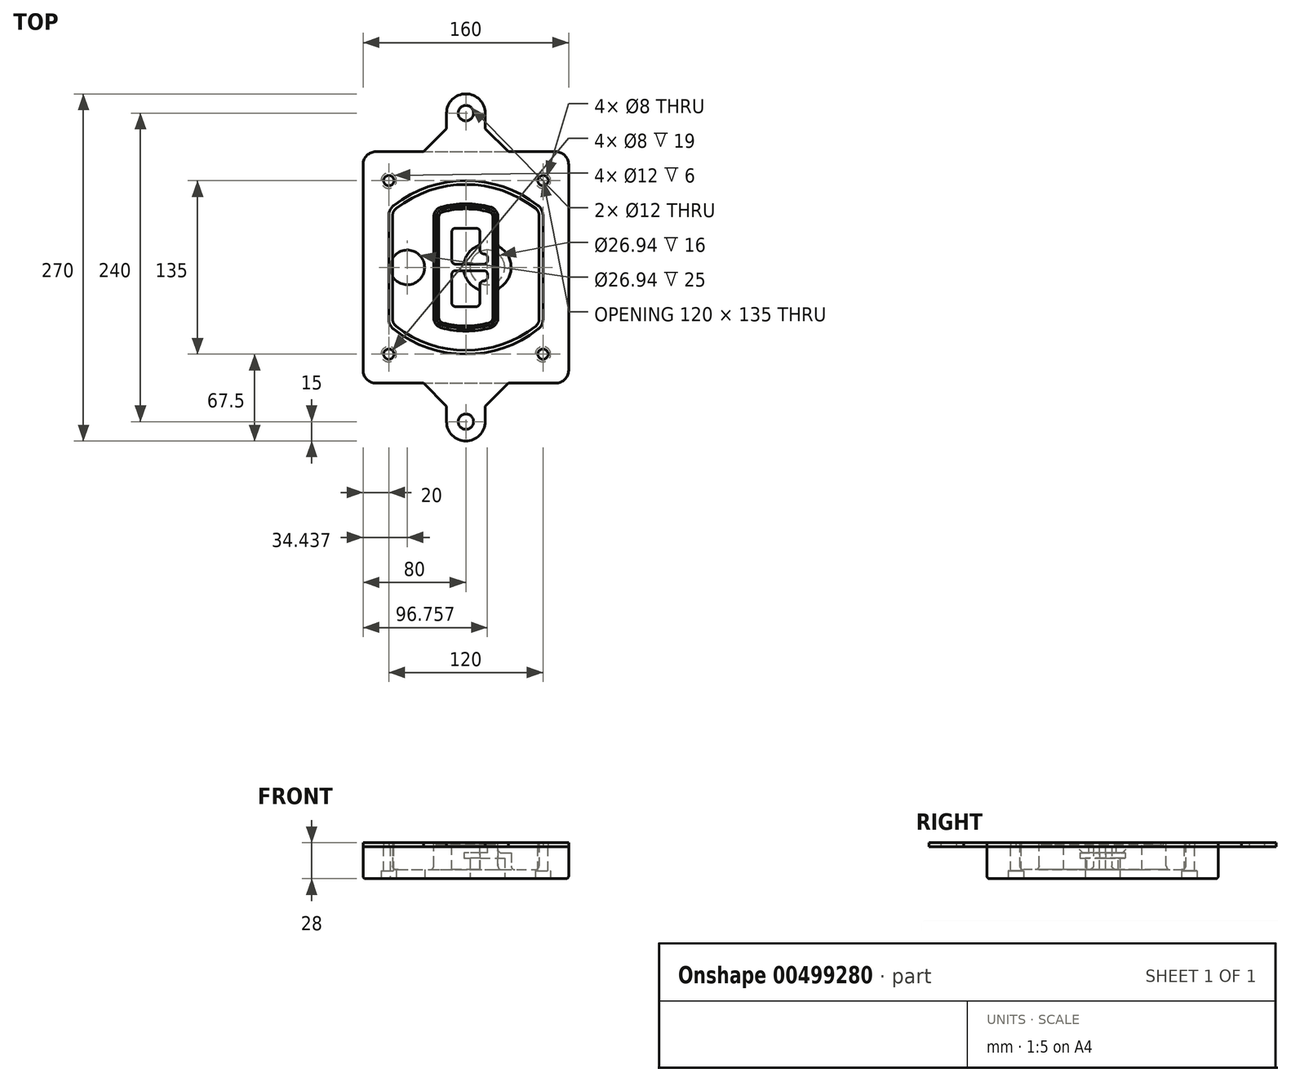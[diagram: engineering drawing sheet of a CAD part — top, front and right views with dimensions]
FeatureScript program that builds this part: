
annotation { "Feature Type Name" : "Feature", "Feature Type Description" : "" }
export const myFeature = defineFeature(function(context is Context, id is Id, definition is map)
    precondition{}
    {
        {
            var Q0;
            Q0=qCreatedBy(makeId("Top.planeOp"),FACE);
            var sketch = newSketch(context, id + "F0", { "sketchPlane" : qUnion([Q0])});
            skPoint(sketch, "E0.rect.middle", {"position": v(0, 0) * mm});
            skLineSegment(sketch, "E1.bottom", {"start": v(-70, -90) * mm, "end": v(70, -90) * mm});
            skLineSegment(sketch, "E1.top", {"start": v(-70, 90) * mm, "end": v(70, 90) * mm});
            skLineSegment(sketch, "E1.left", {"start": v(-80, -80) * mm, "end": v(-80, 80) * mm});
            skLineSegment(sketch, "E1.right", {"start": v(80, -80) * mm, "end": v(80, 80) * mm});
            skLineSegment(sketch, "E2", {"start": v(-80, 90) * mm, "end": v(80, -90) * mm, "construction": true});
            skLineSegment(sketch, "E3", {"start": v(80, 90) * mm, "end": v(-80, -90) * mm, "construction": true});
            skCircle(sketch, "E4", {"center": v(-60, 67.5) * mm, "radius": 4 * mm});
            skCircle(sketch, "E5", {"center": v(60, 67.5) * mm, "radius": 4 * mm});
            skCircle(sketch, "E6", {"center": v(60, -67.5) * mm, "radius": 4 * mm});
            skCircle(sketch, "E7", {"center": v(-60, -67.5) * mm, "radius": 4 * mm});
            skLineSegment(sketch, "E8", {"start": v(-60, 67.5) * mm, "end": v(60, 67.5) * mm, "construction": true});
            skLineSegment(sketch, "E9", {"start": v(60, 67.5) * mm, "end": v(60, -67.5) * mm, "construction": true});
            skLineSegment(sketch, "E10", {"start": v(60, -67.5) * mm, "end": v(-60, -67.5) * mm, "construction": true});
            skLineSegment(sketch, "E11", {"start": v(-60, -67.5) * mm, "end": v(-60, 67.5) * mm, "construction": true});
            skLineSegment(sketch, "E12", {"start": v(-60, 40.3) * mm, "end": v(-60, -40.3) * mm});
            skLineSegment(sketch, "E13", {"start": v(60, 40.3) * mm, "end": v(60, -40.3) * mm});
            skArc(sketch, "E14", {"start": v(56.15, 48.18) * mm, "mid": v(0, 67.5) * mm, "end": v(-56.15, 48.18) * mm});
            skArc(sketch, "E15", {"start": v(-56.15, -48.18) * mm, "mid": v(0, -67.5) * mm, "end": v(56.15, -48.18) * mm});
            skLineSegment(sketch, "E16", {"start": v(-60, 0) * mm, "end": v(60, 0) * mm, "construction": true});
            skPoint(sketch, "E17.visualSharp", {"position": v(-60, -45) * mm});
            skArc(sketch, "E17.filletArc", {"start": v(-60, -40.3) * mm, "mid": v(-58.99, -44.68) * mm, "end": v(-56.15, -48.18) * mm});
            skPoint(sketch, "E18.visualSharp", {"position": v(-60, 45) * mm});
            skArc(sketch, "E18.filletArc", {"start": v(-56.15, 48.18) * mm, "mid": v(-58.99, 44.68) * mm, "end": v(-60, 40.3) * mm});
            skPoint(sketch, "E19.visualSharp", {"position": v(60, 45) * mm});
            skArc(sketch, "E19.filletArc", {"start": v(60, 40.3) * mm, "mid": v(58.99, 44.68) * mm, "end": v(56.15, 48.18) * mm});
            skPoint(sketch, "E20.visualSharp", {"position": v(60, -45) * mm});
            skArc(sketch, "E20.filletArc", {"start": v(56.15, -48.18) * mm, "mid": v(58.99, -44.68) * mm, "end": v(60, -40.3) * mm});
            skPoint(sketch, "E21.visualSharp", {"position": v(-80, 90) * mm});
            skArc(sketch, "E21.filletArc", {"start": v(-70, 90) * mm, "mid": v(-77.07, 87.07) * mm, "end": v(-80, 80) * mm});
            skPoint(sketch, "E22.visualSharp", {"position": v(80, 90) * mm});
            skArc(sketch, "E22.filletArc", {"start": v(80, 80) * mm, "mid": v(77.07, 87.07) * mm, "end": v(70, 90) * mm});
            skPoint(sketch, "E23.visualSharp", {"position": v(80, -90) * mm});
            skArc(sketch, "E23.filletArc", {"start": v(70, -90) * mm, "mid": v(77.07, -87.07) * mm, "end": v(80, -80) * mm});
            skPoint(sketch, "E24.visualSharp", {"position": v(-80, -90) * mm});
            skArc(sketch, "E24.filletArc", {"start": v(-80, -80) * mm, "mid": v(-77.07, -87.07) * mm, "end": v(-70, -90) * mm});
            skArc(sketch, "E25.0", {"start": v(57, 40.3) * mm, "mid": v(56.3, 43.36) * mm, "end": v(54.3, 45.81) * mm});
            skLineSegment(sketch, "E25.1", {"start": v(57, 40.3) * mm, "end": v(57, -40.3) * mm});
            skArc(sketch, "E25.2", {"start": v(54.3, -45.81) * mm, "mid": v(56.3, -43.36) * mm, "end": v(57, -40.3) * mm});
            skArc(sketch, "E25.3", {"start": v(-54.3, -45.81) * mm, "mid": v(0, -64.5) * mm, "end": v(54.3, -45.81) * mm});
            skArc(sketch, "E25.4", {"start": v(-57, -40.3) * mm, "mid": v(-56.3, -43.36) * mm, "end": v(-54.3, -45.81) * mm});
            skArc(sketch, "E25.5", {"start": v(54.3, 45.81) * mm, "mid": v(0, 64.5) * mm, "end": v(-54.3, 45.81) * mm});
            skLineSegment(sketch, "E25.6", {"start": v(-57, 40.3) * mm, "end": v(-57, -40.3) * mm});
            skArc(sketch, "E25.7", {"start": v(-54.3, 45.81) * mm, "mid": v(-56.3, 43.36) * mm, "end": v(-57, 40.3) * mm});
            skArc(sketch, "E26.0", {"start": v(-58.62, 51.33) * mm, "mid": v(-62.58, 46.43) * mm, "end": v(-64, 40.3) * mm});
            skArc(sketch, "E26.1", {"start": v(58.62, 51.33) * mm, "mid": v(0, 71.5) * mm, "end": v(-58.62, 51.33) * mm});
            skArc(sketch, "E26.2", {"start": v(64, 40.3) * mm, "mid": v(62.58, 46.43) * mm, "end": v(58.62, 51.33) * mm});
            skLineSegment(sketch, "E26.3", {"start": v(64, 40.3) * mm, "end": v(64, -40.3) * mm});
            skArc(sketch, "E26.4", {"start": v(58.62, -51.33) * mm, "mid": v(62.58, -46.43) * mm, "end": v(64, -40.3) * mm});
            skLineSegment(sketch, "E26.5", {"start": v(-64, 40.3) * mm, "end": v(-64, -40.3) * mm});
            skArc(sketch, "E26.6", {"start": v(-58.62, -51.33) * mm, "mid": v(0, -71.5) * mm, "end": v(58.62, -51.33) * mm});
            skArc(sketch, "E26.7", {"start": v(-64, -40.3) * mm, "mid": v(-62.58, -46.43) * mm, "end": v(-58.62, -51.33) * mm});
            skSolve(sketch);
        }
        {
            var Q0;
            Q0=makeQuery(id+"F0.imprint","IMPRINT",FACE,{"disambiguationData":[TD([[makeQuery(id+"F0.imprint","IMPRINT",EDGE,{"derivedFrom":sQuery(id+"F0.wireOp",EDGE,"E1.bottom")}),1.0]])]});
            var Q1;
            Q1=makeQuery(id+"F0.imprint","IMPRINT",FACE,{"disambiguationData":[TD([[makeQuery(id+"F0.imprint","IMPRINT",EDGE,{"derivedFrom":sQuery(id+"F0.wireOp",EDGE,"E12")}),1.0]])]});
            var Q2;
            Q2=makeQuery(id+"F0.imprint","IMPRINT",FACE,{"disambiguationData":[TD([[makeQuery(id+"F0.imprint","IMPRINT",EDGE,{"derivedFrom":sQuery(id+"F0.wireOp",EDGE,"E25.0")}),1.0]])]});
            var Q3;
            Q3=makeQuery(id+"F0.imprint","IMPRINT",FACE,{"disambiguationData":[TD([[makeQuery(id+"F0.imprint","IMPRINT",EDGE,{"derivedFrom":sQuery(id+"F0.wireOp",EDGE,"E12")}),-1.0]])]});
            extrude(context, id + "F1", {"entities" : qUnion([Q0, Q1, Q2, Q3]), "oppositeDirection" : true, "depth" : 25 * mm});
        }
        {
            var Q0;
            Q0=makeQuery(id+"F0.imprint","IMPRINT",FACE,{"disambiguationData":[TD([[makeQuery(id+"F0.imprint","IMPRINT",EDGE,{"derivedFrom":sQuery(id+"F0.wireOp",EDGE,"E12")}),1.0]])]});
            extrude(context, id + "F2", {"entities" : qUnion([Q0]), "operationType" : NewBodyOperationType.ADD, "depth" : 3 * mm});
        }
        {
            var Q0;
            Q0=makeQuery(id+"F0.imprint","IMPRINT",FACE,{"disambiguationData":[TD([[makeQuery(id+"F0.imprint","IMPRINT",EDGE,{"derivedFrom":sQuery(id+"F0.wireOp",EDGE,"E25.0")}),1.0]])]});
            extrude(context, id + "F3", {"entities" : qUnion([Q0]), "operationType" : NewBodyOperationType.REMOVE, "oppositeDirection" : true, "depth" : 18 * mm});
        }
        {
            var Q0;
            Q0=makeQuery(id+"F2.opExtrude","CAP_FACE",FACE,{"disambiguationData":[OSD([sQuery(id+"F0.wireOp",EDGE,"E12"),sQuery(id+"F0.wireOp",EDGE,"E13"),sQuery(id+"F0.wireOp",EDGE,"E14"),sQuery(id+"F0.wireOp",EDGE,"E15"),sQuery(id+"F0.wireOp",EDGE,"E17.filletArc"),sQuery(id+"F0.wireOp",EDGE,"E18.filletArc"),sQuery(id+"F0.wireOp",EDGE,"E19.filletArc"),sQuery(id+"F0.wireOp",EDGE,"E20.filletArc"),sQuery(id+"F0.wireOp",EDGE,"E25.0"),sQuery(id+"F0.wireOp",EDGE,"E25.1"),sQuery(id+"F0.wireOp",EDGE,"E25.2"),sQuery(id+"F0.wireOp",EDGE,"E25.3"),sQuery(id+"F0.wireOp",EDGE,"E25.4"),sQuery(id+"F0.wireOp",EDGE,"E25.5"),sQuery(id+"F0.wireOp",EDGE,"E25.6"),sQuery(id+"F0.wireOp",EDGE,"E25.7")])],"isStart":false});
            var sketch = newSketch(context, id + "F4", { "sketchPlane" : qUnion([Q0])});
            skArc(sketch, "E27.0", {"start": v(-19.08, -46.97) * mm, "mid": v(0, -49.5) * mm, "end": v(19.08, -46.97) * mm});
            skArc(sketch, "E28.0", {"start": v(19.08, 46.97) * mm, "mid": v(0, 49.5) * mm, "end": v(-19.08, 46.97) * mm});
            skLineSegment(sketch, "E29", {"start": v(-25, 39.25) * mm, "end": v(-25, -39.25) * mm});
            skLineSegment(sketch, "E30", {"start": v(25, 39.25) * mm, "end": v(25, -39.25) * mm});
            skLineSegment(sketch, "E31", {"start": v(-25, 45.1) * mm, "end": v(25, 45.1) * mm, "construction": true});
            skLineSegment(sketch, "E32", {"start": v(-25, -45.1) * mm, "end": v(25, -45.1) * mm, "construction": true});
            skPoint(sketch, "E33.visualSharp", {"position": v(-25, 45.1) * mm});
            skArc(sketch, "E33.filletArc", {"start": v(-19.08, 46.97) * mm, "mid": v(-23.35, 44.11) * mm, "end": v(-25, 39.25) * mm});
            skPoint(sketch, "E34.visualSharp", {"position": v(25, 45.1) * mm});
            skArc(sketch, "E34.filletArc", {"start": v(25, 39.25) * mm, "mid": v(23.35, 44.11) * mm, "end": v(19.08, 46.97) * mm});
            skPoint(sketch, "E35.visualSharp", {"position": v(25, -45.1) * mm});
            skArc(sketch, "E35.filletArc", {"start": v(19.08, -46.97) * mm, "mid": v(23.35, -44.11) * mm, "end": v(25, -39.25) * mm});
            skPoint(sketch, "E36.visualSharp", {"position": v(-25, -45.1) * mm});
            skArc(sketch, "E36.filletArc", {"start": v(-25, -39.25) * mm, "mid": v(-23.35, -44.11) * mm, "end": v(-19.08, -46.97) * mm});
            skArc(sketch, "E37.0", {"start": v(54.3, 45.81) * mm, "mid": v(0, 64.5) * mm, "end": v(-54.3, 45.81) * mm});
            skArc(sketch, "E37.1", {"start": v(-54.3, 45.81) * mm, "mid": v(-56.3, 43.36) * mm, "end": v(-57, 40.3) * mm});
            skLineSegment(sketch, "E37.2", {"start": v(-57, 40.3) * mm, "end": v(-57, -40.3) * mm});
            skArc(sketch, "E37.3", {"start": v(-57, -40.3) * mm, "mid": v(-56.3, -43.36) * mm, "end": v(-54.3, -45.81) * mm});
            skArc(sketch, "E37.4", {"start": v(-54.3, -45.81) * mm, "mid": v(0, -64.5) * mm, "end": v(54.3, -45.81) * mm});
            skArc(sketch, "E37.5", {"start": v(54.3, -45.81) * mm, "mid": v(56.3, -43.36) * mm, "end": v(57, -40.3) * mm});
            skLineSegment(sketch, "E37.6", {"start": v(57, 40.3) * mm, "end": v(57, -40.3) * mm});
            skArc(sketch, "E37.7", {"start": v(57, 40.3) * mm, "mid": v(56.3, 43.36) * mm, "end": v(54.3, 45.81) * mm});
            skLineSegment(sketch, "E38.0", {"start": v(23, 39.25) * mm, "end": v(23, -39.25) * mm});
            skArc(sketch, "E38.1", {"start": v(18.56, -45.04) * mm, "mid": v(21.76, -42.9) * mm, "end": v(23, -39.25) * mm});
            skArc(sketch, "E38.2", {"start": v(-18.56, -45.04) * mm, "mid": v(0, -47.5) * mm, "end": v(18.56, -45.04) * mm});
            skArc(sketch, "E38.3", {"start": v(-23, -39.25) * mm, "mid": v(-21.76, -42.9) * mm, "end": v(-18.56, -45.04) * mm});
            skLineSegment(sketch, "E38.4", {"start": v(-23, 39.25) * mm, "end": v(-23, -39.25) * mm});
            skArc(sketch, "E38.5", {"start": v(23, 39.25) * mm, "mid": v(21.76, 42.9) * mm, "end": v(18.56, 45.04) * mm});
            skArc(sketch, "E38.6", {"start": v(-18.56, 45.04) * mm, "mid": v(-21.76, 42.9) * mm, "end": v(-23, 39.25) * mm});
            skArc(sketch, "E38.7", {"start": v(18.56, 45.04) * mm, "mid": v(0, 47.5) * mm, "end": v(-18.56, 45.04) * mm});
            skArc(sketch, "E39.0", {"start": v(21, 39.25) * mm, "mid": v(20.18, 41.68) * mm, "end": v(18.04, 43.1) * mm});
            skLineSegment(sketch, "E39.1", {"start": v(21, 39.25) * mm, "end": v(21, -39.25) * mm});
            skArc(sketch, "E39.2", {"start": v(18.04, -43.1) * mm, "mid": v(20.18, -41.68) * mm, "end": v(21, -39.25) * mm});
            skArc(sketch, "E39.3", {"start": v(-18.04, -43.1) * mm, "mid": v(0, -45.5) * mm, "end": v(18.04, -43.1) * mm});
            skArc(sketch, "E39.4", {"start": v(-21, -39.25) * mm, "mid": v(-20.18, -41.68) * mm, "end": v(-18.04, -43.1) * mm});
            skArc(sketch, "E39.5", {"start": v(18.04, 43.1) * mm, "mid": v(0, 45.5) * mm, "end": v(-18.04, 43.1) * mm});
            skLineSegment(sketch, "E39.6", {"start": v(-21, 39.25) * mm, "end": v(-21, -39.25) * mm});
            skArc(sketch, "E39.7", {"start": v(-18.04, 43.1) * mm, "mid": v(-20.18, 41.68) * mm, "end": v(-21, 39.25) * mm});
            skLineSegment(sketch, "E40", {"start": v(-25, 0) * mm, "end": v(25, 0) * mm, "construction": true});
            skLineSegment(sketch, "E41", {"start": v(-11, 5.5) * mm, "end": v(-11, 27.5) * mm});
            skLineSegment(sketch, "E42", {"start": v(-8, 30.5) * mm, "end": v(8, 30.5) * mm});
            skLineSegment(sketch, "E43", {"start": v(11, 27.5) * mm, "end": v(11, 13.5) * mm});
            skLineSegment(sketch, "E44", {"start": v(14, 10.5) * mm, "end": v(14, 10.5) * mm});
            skLineSegment(sketch, "E45", {"start": v(17, 7.5) * mm, "end": v(17, 5.5) * mm});
            skLineSegment(sketch, "E46", {"start": v(14, 2.5) * mm, "end": v(-8, 2.5) * mm});
            skPoint(sketch, "E47.visualSharp", {"position": v(-11, 30.5) * mm});
            skArc(sketch, "E47.filletArc", {"start": v(-8, 30.5) * mm, "mid": v(-10.12, 29.62) * mm, "end": v(-11, 27.5) * mm});
            skPoint(sketch, "E48.visualSharp", {"position": v(11, 30.5) * mm});
            skArc(sketch, "E48.filletArc", {"start": v(11, 27.5) * mm, "mid": v(10.12, 29.62) * mm, "end": v(8, 30.5) * mm});
            skPoint(sketch, "E49.visualSharp", {"position": v(11, 10.5) * mm});
            skArc(sketch, "E49.filletArc", {"start": v(11, 13.5) * mm, "mid": v(11.88, 11.38) * mm, "end": v(14, 10.5) * mm});
            skPoint(sketch, "E50.visualSharp", {"position": v(17, 10.5) * mm});
            skArc(sketch, "E50.filletArc", {"start": v(17, 7.5) * mm, "mid": v(16.12, 9.62) * mm, "end": v(14, 10.5) * mm});
            skPoint(sketch, "E51.visualSharp", {"position": v(17, 2.5) * mm});
            skArc(sketch, "E51.filletArc", {"start": v(14, 2.5) * mm, "mid": v(16.12, 3.38) * mm, "end": v(17, 5.5) * mm});
            skPoint(sketch, "E52.visualSharp", {"position": v(-11, 2.5) * mm});
            skArc(sketch, "E52.filletArc", {"start": v(-11, 5.5) * mm, "mid": v(-10.12, 3.38) * mm, "end": v(-8, 2.5) * mm});
            skLineSegment(sketch, "E53.0.MirrorCS", {"start": v(14, -2.5) * mm, "end": v(-8, -2.5) * mm});
            skArc(sketch, "E54.0.MirrorCS", {"start": v(-11, -5.5) * mm, "mid": v(-10.12, -3.38) * mm, "end": v(-8, -2.5) * mm});
            skLineSegment(sketch, "E55.0.MirrorCS", {"start": v(-11, -5.5) * mm, "end": v(-11, -27.5) * mm});
            skArc(sketch, "E56.0.MirrorCS", {"start": v(-8, -30.5) * mm, "mid": v(-10.12, -29.62) * mm, "end": v(-11, -27.5) * mm});
            skLineSegment(sketch, "E57.0.MirrorCS", {"start": v(-8, -30.5) * mm, "end": v(8, -30.5) * mm});
            skArc(sketch, "E58.0.MirrorCS", {"start": v(11, -27.5) * mm, "mid": v(10.12, -29.62) * mm, "end": v(8, -30.5) * mm});
            skLineSegment(sketch, "E59.0.MirrorCS", {"start": v(11, -27.5) * mm, "end": v(11, -13.5) * mm});
            skArc(sketch, "E60.0.MirrorCS", {"start": v(11, -13.5) * mm, "mid": v(11.88, -11.38) * mm, "end": v(14, -10.5) * mm});
            skArc(sketch, "E61.0.MirrorCS", {"start": v(17, -7.5) * mm, "mid": v(16.12, -9.62) * mm, "end": v(14, -10.5) * mm});
            skLineSegment(sketch, "E62.0.MirrorCS", {"start": v(17, -7.5) * mm, "end": v(17, -5.5) * mm});
            skArc(sketch, "E63.0.MirrorCS", {"start": v(14, -2.5) * mm, "mid": v(16.12, -3.38) * mm, "end": v(17, -5.5) * mm});
            skSolve(sketch);
        }
        {
            var Q0;
            Q0=makeQuery(id+"F4.imprint","IMPRINT",FACE,{"disambiguationData":[TD([[makeQuery(id+"F4.imprint","IMPRINT",EDGE,{"derivedFrom":sQuery(id+"F4.wireOp",EDGE,"E27.0")}),1.0]])]});
            var Q1;
            Q1=makeQuery(id+"F4.imprint","IMPRINT",FACE,{"disambiguationData":[TD([[makeQuery(id+"F4.imprint","IMPRINT",EDGE,{"derivedFrom":sQuery(id+"F4.wireOp",EDGE,"E38.0")}),-1.0]])]});
            var Q2;
            Q2=makeQuery(id+"F4.imprint","IMPRINT",FACE,{"disambiguationData":[TD([[makeQuery(id+"F4.imprint","IMPRINT",EDGE,{"derivedFrom":sQuery(id+"F4.wireOp",EDGE,"E39.0")}),1.0]])]});
            extrude(context, id + "F5", {"entities" : qUnion([Q0, Q1, Q2]), "operationType" : NewBodyOperationType.ADD, "endBound" : BoundingType.UP_TO_NEXT, "oppositeDirection" : true, "depth" : 25 * mm});
        }
        {
            var Q0;
            Q0=makeQuery(id+"F4.imprint","IMPRINT",FACE,{"disambiguationData":[TD([[makeQuery(id+"F4.imprint","IMPRINT",EDGE,{"derivedFrom":sQuery(id+"F4.wireOp",EDGE,"E38.0")}),-1.0]])]});
            extrude(context, id + "F6", {"entities" : qUnion([Q0]), "operationType" : NewBodyOperationType.REMOVE, "oppositeDirection" : true, "depth" : 2 * mm});
        }
        {
            var Q0;
            Q0=makeQuery(id+"F1.opExtrude","CAP_FACE",FACE,{"disambiguationData":[OSD([sQuery(id+"F0.wireOp",EDGE,"E1.bottom"),sQuery(id+"F0.wireOp",EDGE,"E1.top"),sQuery(id+"F0.wireOp",EDGE,"E1.left"),sQuery(id+"F0.wireOp",EDGE,"E1.right"),sQuery(id+"F0.wireOp",EDGE,"E4"),sQuery(id+"F0.wireOp",EDGE,"E5"),sQuery(id+"F0.wireOp",EDGE,"E6"),sQuery(id+"F0.wireOp",EDGE,"E7"),sQuery(id+"F0.wireOp",EDGE,"E21.filletArc"),sQuery(id+"F0.wireOp",EDGE,"E22.filletArc"),sQuery(id+"F0.wireOp",EDGE,"E23.filletArc"),sQuery(id+"F0.wireOp",EDGE,"E24.filletArc")])],"isStart":false});
            var sketch = newSketch(context, id + "F7", { "sketchPlane" : qUnion([Q0])});
            skCircle(sketch, "E64", {"center": v(16.76, 0) * mm, "radius": 13.47 * mm});
            skCircle(sketch, "E65", {"center": v(-45.56, 0) * mm, "radius": 13.47 * mm});
            skLineSegment(sketch, "E66", {"start": v(80, 0) * mm, "end": v(-80, 0) * mm});
            skCircle(sketch, "E67", {"center": v(16.76, 0) * mm, "radius": 18.47 * mm});
            skCircle(sketch, "E68", {"center": v(60, -67.5) * mm, "radius": 6 * mm});
            skCircle(sketch, "E69", {"center": v(-60, -67.5) * mm, "radius": 6 * mm});
            skCircle(sketch, "E70", {"center": v(-60, 67.5) * mm, "radius": 6 * mm});
            skCircle(sketch, "E71", {"center": v(60, 67.5) * mm, "radius": 6 * mm});
            skSolve(sketch);
        }
        {
            var Q0;
            {var subQ1=sQuery(id+"F7.wireOp",EDGE,"E66");var subQ4=sQuery(id+"F7.wireOp",EDGE,"E64");var subQ6=makeQuery(id+"F7.imprint","INTERSECT",VERTEX,{"disambiguationData":[OD(0.0)],"derivedFrom":[subQ4,subQ1]});Q0=makeQuery(id+"F7.imprint","IMPRINT",FACE,{"disambiguationData":[TD([[makeQuery(id+"F7.imprint","IMPRINT",EDGE,{"disambiguationData":[TD([[subQ6,-1.0]])],"derivedFrom":subQ4}),-1.0]])]});}
            var Q1;
            {var subQ0=sQuery(id+"F7.wireOp",EDGE,"E66");var subQ1=sQuery(id+"F7.wireOp",EDGE,"E64");var subQ3=makeQuery(id+"F7.imprint","INTERSECT",VERTEX,{"disambiguationData":[OD(0.0)],"derivedFrom":[subQ1,subQ0]});Q1=makeQuery(id+"F7.imprint","IMPRINT",FACE,{"disambiguationData":[TD([[makeQuery(id+"F7.imprint","IMPRINT",EDGE,{"disambiguationData":[TD([[subQ3,-1.0]])],"derivedFrom":subQ1}),1.0]])]});}
            var Q2;
            {var subQ0=sQuery(id+"F7.wireOp",EDGE,"E66");var subQ1=sQuery(id+"F7.wireOp",EDGE,"E64");var subQ3=makeQuery(id+"F7.imprint","INTERSECT",VERTEX,{"disambiguationData":[OD(0.0)],"derivedFrom":[subQ1,subQ0]});Q2=makeQuery(id+"F7.imprint","IMPRINT",FACE,{"disambiguationData":[TD([[makeQuery(id+"F7.imprint","IMPRINT",EDGE,{"disambiguationData":[TD([[subQ3,1.0]])],"derivedFrom":subQ1}),1.0]])]});}
            var Q3;
            {var subQ1=sQuery(id+"F7.wireOp",EDGE,"E66");var subQ4=sQuery(id+"F7.wireOp",EDGE,"E64");var subQ6=makeQuery(id+"F7.imprint","INTERSECT",VERTEX,{"disambiguationData":[OD(0.0)],"derivedFrom":[subQ4,subQ1]});Q3=makeQuery(id+"F7.imprint","IMPRINT",FACE,{"disambiguationData":[TD([[makeQuery(id+"F7.imprint","IMPRINT",EDGE,{"disambiguationData":[TD([[subQ6,1.0]])],"derivedFrom":subQ4}),-1.0]])]});}
            extrude(context, id + "F8", {"entities" : qUnion([Q0, Q1, Q2, Q3]), "operationType" : NewBodyOperationType.ADD, "oppositeDirection" : true, "depth" : 20 * mm});
        }
        {
            var Q0;
            {var subQ0=sQuery(id+"F7.wireOp",EDGE,"E66");var subQ1=sQuery(id+"F7.wireOp",EDGE,"E64");var subQ3=makeQuery(id+"F7.imprint","INTERSECT",VERTEX,{"disambiguationData":[OD(0.0)],"derivedFrom":[subQ1,subQ0]});Q0=makeQuery(id+"F7.imprint","IMPRINT",FACE,{"disambiguationData":[TD([[makeQuery(id+"F7.imprint","IMPRINT",EDGE,{"disambiguationData":[TD([[subQ3,-1.0]])],"derivedFrom":subQ1}),1.0]])]});}
            var Q1;
            {var subQ0=sQuery(id+"F7.wireOp",EDGE,"E66");var subQ1=sQuery(id+"F7.wireOp",EDGE,"E64");var subQ3=makeQuery(id+"F7.imprint","INTERSECT",VERTEX,{"disambiguationData":[OD(0.0)],"derivedFrom":[subQ1,subQ0]});Q1=makeQuery(id+"F7.imprint","IMPRINT",FACE,{"disambiguationData":[TD([[makeQuery(id+"F7.imprint","IMPRINT",EDGE,{"disambiguationData":[TD([[subQ3,1.0]])],"derivedFrom":subQ1}),1.0]])]});}
            extrude(context, id + "F9", {"entities" : qUnion([Q0, Q1]), "operationType" : NewBodyOperationType.REMOVE, "oppositeDirection" : true, "depth" : 16 * mm});
        }
        {
            var Q0;
            {var subQ0=sQuery(id+"F7.wireOp",EDGE,"E66");var subQ1=sQuery(id+"F7.wireOp",EDGE,"E65");var subQ3=makeQuery(id+"F7.imprint","INTERSECT",VERTEX,{"disambiguationData":[OD(0.0)],"derivedFrom":[subQ1,subQ0]});Q0=makeQuery(id+"F7.imprint","IMPRINT",FACE,{"disambiguationData":[TD([[makeQuery(id+"F7.imprint","IMPRINT",EDGE,{"disambiguationData":[TD([[subQ3,-1.0]])],"derivedFrom":subQ1}),1.0]])]});}
            var Q1;
            {var subQ0=sQuery(id+"F7.wireOp",EDGE,"E66");var subQ1=sQuery(id+"F7.wireOp",EDGE,"E65");var subQ3=makeQuery(id+"F7.imprint","INTERSECT",VERTEX,{"disambiguationData":[OD(0.0)],"derivedFrom":[subQ1,subQ0]});Q1=makeQuery(id+"F7.imprint","IMPRINT",FACE,{"disambiguationData":[TD([[makeQuery(id+"F7.imprint","IMPRINT",EDGE,{"disambiguationData":[TD([[subQ3,1.0]])],"derivedFrom":subQ1}),1.0]])]});}
            extrude(context, id + "F10", {"entities" : qUnion([Q0, Q1]), "operationType" : NewBodyOperationType.REMOVE, "oppositeDirection" : true, "depth" : 25 * mm});
        }
        {
            var Q0;
            Q0=makeQuery(id+"F7.imprint","IMPRINT",FACE,{"disambiguationData":[TD([[makeQuery(id+"F7.imprint","IMPRINT",EDGE,{"derivedFrom":sQuery(id+"F7.wireOp",EDGE,"E68")}),1.0]])]});
            var Q1;
            Q1=makeQuery(id+"F7.imprint","IMPRINT",FACE,{"disambiguationData":[TD([[makeQuery(id+"F7.imprint","IMPRINT",EDGE,{"derivedFrom":makeQuery(id+"F1.opExtrude","CAP_EDGE",EDGE,{"disambiguationData":[OSD([sQuery(id+"F0.wireOp",EDGE,"E5")])],"isStart":false})}),-1.0]])]});
            var Q2;
            Q2=makeQuery(id+"F7.imprint","IMPRINT",FACE,{"disambiguationData":[TD([[makeQuery(id+"F7.imprint","IMPRINT",EDGE,{"derivedFrom":sQuery(id+"F7.wireOp",EDGE,"E69")}),1.0]])]});
            var Q3;
            Q3=makeQuery(id+"F7.imprint","IMPRINT",FACE,{"disambiguationData":[TD([[makeQuery(id+"F7.imprint","IMPRINT",EDGE,{"derivedFrom":makeQuery(id+"F1.opExtrude","CAP_EDGE",EDGE,{"disambiguationData":[OSD([sQuery(id+"F0.wireOp",EDGE,"E4")])],"isStart":false})}),-1.0]])]});
            var Q4;
            Q4=makeQuery(id+"F7.imprint","IMPRINT",FACE,{"disambiguationData":[TD([[makeQuery(id+"F7.imprint","IMPRINT",EDGE,{"derivedFrom":sQuery(id+"F7.wireOp",EDGE,"E70")}),1.0]])]});
            var Q5;
            Q5=makeQuery(id+"F7.imprint","IMPRINT",FACE,{"disambiguationData":[TD([[makeQuery(id+"F7.imprint","IMPRINT",EDGE,{"derivedFrom":makeQuery(id+"F1.opExtrude","CAP_EDGE",EDGE,{"disambiguationData":[OSD([sQuery(id+"F0.wireOp",EDGE,"E7")])],"isStart":false})}),-1.0]])]});
            var Q6;
            Q6=makeQuery(id+"F7.imprint","IMPRINT",FACE,{"disambiguationData":[TD([[makeQuery(id+"F7.imprint","IMPRINT",EDGE,{"derivedFrom":sQuery(id+"F7.wireOp",EDGE,"E71")}),1.0]])]});
            var Q7;
            Q7=makeQuery(id+"F7.imprint","IMPRINT",FACE,{"disambiguationData":[TD([[makeQuery(id+"F7.imprint","IMPRINT",EDGE,{"derivedFrom":makeQuery(id+"F1.opExtrude","CAP_EDGE",EDGE,{"disambiguationData":[OSD([sQuery(id+"F0.wireOp",EDGE,"E6")])],"isStart":false})}),-1.0]])]});
            extrude(context, id + "F11", {"entities" : qUnion([Q0, Q1, Q2, Q3, Q4, Q5, Q6, Q7]), "operationType" : NewBodyOperationType.REMOVE, "oppositeDirection" : true, "depth" : 6 * mm});
        }
        {
            var Q0;
            Q0=makeQuery(id+"F9.boolean.opBoolean","COPY",FACE,{"derivedFrom":makeQuery(id+"F9.opExtrude","CAP_FACE",FACE,{"disambiguationData":[OSD([sQuery(id+"F7.wireOp",EDGE,"E64")])],"isStart":false})});
            var sketch = newSketch(context, id + "F12", { "sketchPlane" : qUnion([Q0])});
            skArc(sketch, "E72.0", {"start": v(11, 17.55) * mm, "mid": v(2.57, 11.82) * mm, "end": v(-1.54, 2.5) * mm});
            skArc(sketch, "E72.1", {"start": v(-1.54, -2.5) * mm, "mid": v(2.57, -11.82) * mm, "end": v(11, -17.55) * mm});
            skLineSegment(sketch, "E73", {"start": v(-1.54, -2.5) * mm, "end": v(14, -2.5) * mm});
            skLineSegment(sketch, "E74.0", {"start": v(14, 2.5) * mm, "end": v(-1.54, 2.5) * mm});
            skArc(sketch, "E74.1", {"start": v(14, 2.5) * mm, "mid": v(16.12, 3.38) * mm, "end": v(17, 5.5) * mm});
            skLineSegment(sketch, "E74.2", {"start": v(17, 7.5) * mm, "end": v(17, 5.5) * mm});
            skArc(sketch, "E74.3", {"start": v(17, 7.5) * mm, "mid": v(16.12, 9.62) * mm, "end": v(14, 10.5) * mm});
            skArc(sketch, "E74.4", {"start": v(11, 13.5) * mm, "mid": v(11.88, 11.38) * mm, "end": v(14, 10.5) * mm});
            skLineSegment(sketch, "E74.5", {"start": v(11, 17.55) * mm, "end": v(11, 13.5) * mm});
            skLineSegment(sketch, "E74.7", {"start": v(14, -2.5) * mm, "end": v(-1.54, -2.5) * mm});
            skArc(sketch, "E74.8", {"start": v(14, -2.5) * mm, "mid": v(16.12, -3.38) * mm, "end": v(17, -5.5) * mm});
            skLineSegment(sketch, "E74.9", {"start": v(17, -7.5) * mm, "end": v(17, -5.5) * mm});
            skArc(sketch, "E74.10", {"start": v(17, -7.5) * mm, "mid": v(16.12, -9.62) * mm, "end": v(14, -10.5) * mm});
            skArc(sketch, "E74.11", {"start": v(11, -13.5) * mm, "mid": v(11.88, -11.38) * mm, "end": v(14, -10.5) * mm});
            skLineSegment(sketch, "E74.12", {"start": v(11, -17.55) * mm, "end": v(11, -13.5) * mm});
            skPoint(sketch, "E75.orphan", {"position": v(11, -27.5) * mm});
            skPoint(sketch, "E76.orphan", {"position": v(-8, -2.5) * mm});
            skPoint(sketch, "E77.orphan", {"position": v(-8, 2.5) * mm});
            skPoint(sketch, "E78.orphan", {"position": v(11, 27.5) * mm});
            skSolve(sketch);
        }
        {
            var Q0;
            {var subQ7=sQuery(id+"F12.wireOp",EDGE,"E72.0");var subQ14=sQuery(id+"F12.wireOp",EDGE,"E72.1");var subQ16=sQuery(id+"F12.wireOp",EDGE,"E74.1");var subQ18=sQuery(id+"F12.wireOp",EDGE,"E74.8");Q0=qUnion([makeQuery(id+"F12.imprint","IMPRINT",FACE,{"disambiguationData":[TD([[makeQuery(id+"F12.imprint","IMPRINT",EDGE,{"derivedFrom":subQ7}),1.0]])]}),makeQuery(id+"F12.imprint","IMPRINT",FACE,{"disambiguationData":[TD([[makeQuery(id+"F12.imprint","IMPRINT",EDGE,{"derivedFrom":subQ14}),1.0]])]}),makeQuery(id+"F12.imprint","IMPRINT",FACE,{"disambiguationData":[TD([[makeQuery(id+"F12.imprint","IMPRINT",EDGE,{"derivedFrom":subQ16}),1.0]])]}),makeQuery(id+"F12.imprint","IMPRINT",FACE,{"disambiguationData":[TD([[makeQuery(id+"F12.imprint","IMPRINT",EDGE,{"derivedFrom":subQ18}),-1.0]])]})]);}
            var Q1;
            Q1=makeQuery(id+"F5.boolean.opBoolean","SPLIT",FACE,{"disambiguationData":[TD([makeQuery(id+"F5.opExtrude","SWEPT_FACE",FACE,{"disambiguationData":[OSD([sQuery(id+"F4.wireOp",EDGE,"E41")])]})])],"derivedFrom":makeQuery(id+"F3.boolean.opBoolean","COPY",FACE,{"derivedFrom":makeQuery(id+"F3.opExtrude","CAP_FACE",FACE,{"disambiguationData":[OSD([sQuery(id+"F0.wireOp",EDGE,"E25.0"),sQuery(id+"F0.wireOp",EDGE,"E25.1"),sQuery(id+"F0.wireOp",EDGE,"E25.2"),sQuery(id+"F0.wireOp",EDGE,"E25.3"),sQuery(id+"F0.wireOp",EDGE,"E25.4"),sQuery(id+"F0.wireOp",EDGE,"E25.5"),sQuery(id+"F0.wireOp",EDGE,"E25.6"),sQuery(id+"F0.wireOp",EDGE,"E25.7")])],"isStart":false})})});
            extrude(context, id + "F13", {"entities" : qUnion([Q0]), "operationType" : NewBodyOperationType.REMOVE, "endBound" : BoundingType.UP_TO_SURFACE, "endBoundEntityFace" : qUnion([Q1]), "depth" : 25 * mm});
        }
        {
            var Q0;
            Q0=makeQuery(id+"F3.boolean.opBoolean","COPY",EDGE,{"derivedFrom":makeQuery(id+"F3.opExtrude","CAP_EDGE",EDGE,{"disambiguationData":[OSD([sQuery(id+"F0.wireOp",EDGE,"E25.6")])],"isStart":false})});
            var Q1;
            Q1=makeQuery(id+"F8.boolean.opBoolean","INTERSECT",EDGE,{"derivedFrom":[makeQuery(id+"F5.opExtrude","SWEPT_FACE",FACE,{"disambiguationData":[OSD([sQuery(id+"F4.wireOp",EDGE,"E30")])]}),makeQuery(id+"F8.opExtrude","CAP_FACE",FACE,{"disambiguationData":[OSD([sQuery(id+"F7.wireOp",EDGE,"E67")])],"isStart":false})]});
            var Q2;
            Q2=makeQuery(id+"F8.boolean.opBoolean","INTERSECT",EDGE,{"disambiguationData":[OD(1.0)],"derivedFrom":[makeQuery(id+"F5.opExtrude","SWEPT_FACE",FACE,{"disambiguationData":[OSD([sQuery(id+"F4.wireOp",EDGE,"E30")])]}),makeQuery(id+"F8.opExtrude","SWEPT_FACE",FACE,{"disambiguationData":[OSD([sQuery(id+"F7.wireOp",EDGE,"E67")])]})]});
            var Q3;
            {var subQ0=sQuery(id+"F4.wireOp",EDGE,"E30");Q3=makeQuery(id+"F8.boolean.opBoolean","SPLIT",EDGE,{"disambiguationData":[TD([makeQuery(id+"F5.opExtrude","SWEPT_FACE",FACE,{"disambiguationData":[OSD([sQuery(id+"F4.wireOp",EDGE,"E35.filletArc")])]})])],"derivedFrom":makeQuery(id+"F5.opExtrude","CAP_EDGE",EDGE,{"disambiguationData":[OSD([subQ0])],"isStart":false})});}
            var Q4;
            {var subQ0=sQuery(id+"F0.wireOp",EDGE,"E25.7");var subQ1=sQuery(id+"F0.wireOp",EDGE,"E25.1");var subQ2=sQuery(id+"F0.wireOp",EDGE,"E25.6");var subQ3=sQuery(id+"F0.wireOp",EDGE,"E25.5");var subQ4=sQuery(id+"F0.wireOp",EDGE,"E25.4");var subQ5=sQuery(id+"F0.wireOp",EDGE,"E25.0");var subQ6=sQuery(id+"F0.wireOp",EDGE,"E25.2");var subQ7=sQuery(id+"F0.wireOp",EDGE,"E25.3");Q4=makeQuery(id+"F8.boolean.opBoolean","INTERSECT",EDGE,{"derivedFrom":[makeQuery(id+"F5.boolean.opBoolean","SPLIT",FACE,{"disambiguationData":[TD([makeQuery(id+"F2.opExtrude","SWEPT_FACE",FACE,{"disambiguationData":[OSD([subQ5])]})])],"derivedFrom":makeQuery(id+"F3.boolean.opBoolean","COPY",FACE,{"derivedFrom":makeQuery(id+"F3.opExtrude","CAP_FACE",FACE,{"disambiguationData":[OSD([subQ5,subQ1,subQ6,subQ7,subQ4,subQ3,subQ2,subQ0])],"isStart":false})})}),makeQuery(id+"F8.opExtrude","SWEPT_FACE",FACE,{"disambiguationData":[OSD([sQuery(id+"F7.wireOp",EDGE,"E67")])]})]});}
            var Q5;
            Q5=makeQuery(id+"F8.boolean.opBoolean","INTERSECT",EDGE,{"disambiguationData":[OD(0.0)],"derivedFrom":[makeQuery(id+"F5.opExtrude","SWEPT_FACE",FACE,{"disambiguationData":[OSD([sQuery(id+"F4.wireOp",EDGE,"E30")])]}),makeQuery(id+"F8.opExtrude","SWEPT_FACE",FACE,{"disambiguationData":[OSD([sQuery(id+"F7.wireOp",EDGE,"E67")])]})]});
            fillet(context, id + "F14", {"entities" : qUnion([Q0, Q1, Q2, Q3, Q4, Q5]), "radius" : 3 * mm, "tangentPropagation" : true, "allowEdgeOverflow" : false});
        }
        {
            var Q0;
            Q0=makeQuery(id+"F1.opExtrude","CAP_EDGE",EDGE,{"disambiguationData":[OSD([sQuery(id+"F0.wireOp",EDGE,"E1.bottom")])],"isStart":false});
            fillet(context, id + "F15", {"entities" : qUnion([Q0]), "radius" : 2 * mm, "tangentPropagation" : true, "allowEdgeOverflow" : false});
        }
        {
            var Q0;
            {var subQ0=sQuery(id+"F0.wireOp",EDGE,"E21.filletArc");var subQ1=sQuery(id+"F0.wireOp",EDGE,"E7");var subQ2=sQuery(id+"F0.wireOp",EDGE,"E6");var subQ3=sQuery(id+"F0.wireOp",EDGE,"E5");var subQ4=sQuery(id+"F0.wireOp",EDGE,"E4");var subQ5=sQuery(id+"F0.wireOp",EDGE,"E22.filletArc");var subQ6=sQuery(id+"F0.wireOp",EDGE,"E1.bottom");var subQ7=sQuery(id+"F0.wireOp",EDGE,"E1.right");var subQ8=sQuery(id+"F0.wireOp",EDGE,"E1.top");var subQ9=sQuery(id+"F0.wireOp",EDGE,"E1.left");var subQ10=sQuery(id+"F0.wireOp",EDGE,"E23.filletArc");var subQ11=sQuery(id+"F0.wireOp",EDGE,"E24.filletArc");Q0=makeQuery(id+"F2.boolean.opBoolean","SPLIT",FACE,{"disambiguationData":[TD([makeQuery(id+"F1.opExtrude","SWEPT_FACE",FACE,{"disambiguationData":[OSD([subQ6])]})])],"derivedFrom":makeQuery(id+"F1.opExtrude","CAP_FACE",FACE,{"disambiguationData":[OSD([subQ6,subQ8,subQ9,subQ7,subQ4,subQ3,subQ2,subQ1,subQ0,subQ5,subQ10,subQ11])],"isStart":true})});}
            var sketch = newSketch(context, id + "F16", { "sketchPlane" : qUnion([Q0])});
            skLineSegment(sketch, "E79", {"start": v(0, 90) * mm, "end": v(0, 120) * mm, "construction": true});
            skCircle(sketch, "E80", {"center": v(0, 120) * mm, "radius": 6 * mm});
            skLineSegment(sketch, "E81", {"start": v(-33, 90) * mm, "end": v(-15, 108) * mm});
            skLineSegment(sketch, "E82", {"start": v(-15, 108) * mm, "end": v(-15, 120) * mm});
            skLineSegment(sketch, "E83", {"start": v(33, 90) * mm, "end": v(15, 108) * mm});
            skLineSegment(sketch, "E84", {"start": v(15, 108) * mm, "end": v(15, 120) * mm});
            skArc(sketch, "E85", {"start": v(15, 120) * mm, "mid": v(0, 135) * mm, "end": v(-15, 120) * mm});
            skArc(sketch, "E86.MirrorCS", {"start": v(-15, 120) * mm, "mid": v(0, 135) * mm, "end": v(15, 120) * mm});
            skLineSegment(sketch, "E87", {"start": v(-80, 0) * mm, "end": v(80, 0) * mm, "construction": true});
            skLineSegment(sketch, "E88.MirrorCS", {"start": v(-33, -90) * mm, "end": v(-15, -108) * mm});
            skLineSegment(sketch, "E89.MirrorCS", {"start": v(-15, -108) * mm, "end": v(-15, -120) * mm});
            skArc(sketch, "E90.MirrorCS", {"start": v(15, -120) * mm, "mid": v(0, -135) * mm, "end": v(-15, -120) * mm});
            skCircle(sketch, "E91.MirrorC", {"center": v(0, -120) * mm, "radius": 6 * mm});
            skLineSegment(sketch, "E92.MirrorCS", {"start": v(0, -90) * mm, "end": v(0, -120) * mm, "construction": true});
            skLineSegment(sketch, "E93.MirrorCS", {"start": v(15, -108) * mm, "end": v(15, -120) * mm});
            skLineSegment(sketch, "E94.MirrorCS", {"start": v(33, -90) * mm, "end": v(15, -108) * mm});
            skSolve(sketch);
        }
        {
            var Q0;
            Q0=makeQuery(id+"F16.imprint","IMPRINT",FACE,{"disambiguationData":[TD([[makeQuery(id+"F16.imprint","IMPRINT",EDGE,{"derivedFrom":makeQuery(id+"F1.opExtrude","CAP_EDGE",EDGE,{"disambiguationData":[OSD([sQuery(id+"F0.wireOp",EDGE,"E1.left")])],"isStart":true})}),-1.0]])]});
            var Q1;
            Q1=makeQuery(id+"F16.imprint","IMPRINT",FACE,{"disambiguationData":[TD([[makeQuery(id+"F16.imprint","IMPRINT",EDGE,{"derivedFrom":sQuery(id+"F16.wireOp",EDGE,"E80")}),-1.0]])]});
            var Q2;
            {var subQ0=sQuery(id+"F16.wireOp",EDGE,"E88.MirrorCS");Q2=makeQuery(id+"F16.imprint","IMPRINT",FACE,{"disambiguationData":[TD([[makeQuery(id+"F16.imprint","IMPRINT",EDGE,{"derivedFrom":subQ0}),1.0]])]});}
            var Q3;
            Q3=makeQuery(id+"F2.opExtrude","CAP_FACE",FACE,{"disambiguationData":[OSD([sQuery(id+"F0.wireOp",EDGE,"E12"),sQuery(id+"F0.wireOp",EDGE,"E13"),sQuery(id+"F0.wireOp",EDGE,"E14"),sQuery(id+"F0.wireOp",EDGE,"E15"),sQuery(id+"F0.wireOp",EDGE,"E17.filletArc"),sQuery(id+"F0.wireOp",EDGE,"E18.filletArc"),sQuery(id+"F0.wireOp",EDGE,"E19.filletArc"),sQuery(id+"F0.wireOp",EDGE,"E20.filletArc"),sQuery(id+"F0.wireOp",EDGE,"E25.0"),sQuery(id+"F0.wireOp",EDGE,"E25.1"),sQuery(id+"F0.wireOp",EDGE,"E25.2"),sQuery(id+"F0.wireOp",EDGE,"E25.3"),sQuery(id+"F0.wireOp",EDGE,"E25.4"),sQuery(id+"F0.wireOp",EDGE,"E25.5"),sQuery(id+"F0.wireOp",EDGE,"E25.6"),sQuery(id+"F0.wireOp",EDGE,"E25.7")])],"isStart":false});
            extrude(context, id + "F17", {"entities" : qUnion([Q0, Q1, Q2]), "endBound" : BoundingType.UP_TO_SURFACE, "endBoundEntityFace" : qUnion([Q3]), "depth" : 25 * mm});
        }
    });
